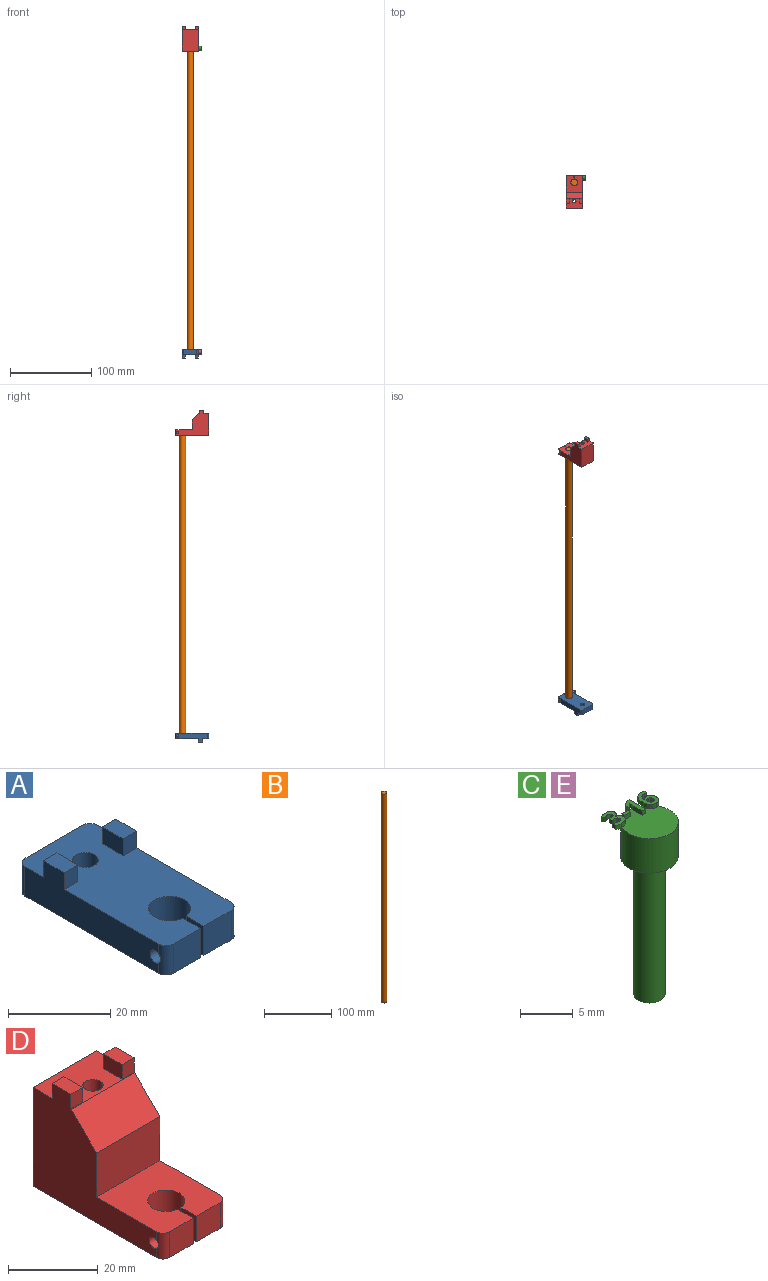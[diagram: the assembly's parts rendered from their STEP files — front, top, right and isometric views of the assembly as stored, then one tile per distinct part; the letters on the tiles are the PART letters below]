
ASSEMBLY  parts=5 mates=4
PART A: 25 faces, bbox 20x41x11 mm
  f0: plane 41x20mm, normal (0,0,1), area 694.2mm2, adj f1,f2,f3,f4,f5,f6,f7,f8
  f1: plane 16x7mm, normal (0,1,0), area 112mm2, adj f0,f10,f21,f24
  f2: plane 37x11mm, normal (-1,0,0), area 276.4mm2, adj f0,f10,f11,f13,f14,f20,f21,f22
  f3: plane 7.5x7mm, normal (0,-1,0), area 52.5mm2, adj f0,f4,f10,f22
  f4: plane 7x4.88mm, normal (1,0,0), area 27.6mm2, adj f0,f3,f5,f10,f20
  f5: cylinder r=4.15mm len=8.3mm, axis (0,0,-1), area 175.5mm2, adj f0,f4,f6,f10
  f6: plane 7x4.88mm, normal (-1,0,0), area 27.6mm2, adj f0,f5,f7,f10,f19
  f7: plane 7.5x7mm, normal (0,-1,0), area 52.5mm2, adj f0,f6,f10,f23
  f8: cylinder r=2.52mm len=7mm, axis (0,0,-1), area 110.8mm2, adj f0,f10
  f9: plane 37x11mm, normal (1,0,0), area 276.4mm2, adj f0,f10,f15,f16,f18,f19,f23,f24
  f10: plane 41x20mm, normal (0,0,-1), area 737.7mm2, adj f1,f2,f3,f4,f5,f6,f7,f8
  f11: plane 4x3.75mm, normal (0,-1,0), area 15mm2, adj f0,f2,f12,f14
  f12: plane 5.8x4mm, normal (1,0,0), area 23.2mm2, adj f0,f11,f13,f14
  f13: plane 4x3.75mm, normal (0,1,0), area 15mm2, adj f0,f2,f12,f14
  f14: plane 5.8x3.75mm, normal (0,0,1), area 21.7mm2, adj f2,f11,f12,f13
  f15: plane 4x3.75mm, normal (0,-1,0), area 15mm2, adj f0,f9,f17,f18
  f16: plane 4x3.75mm, normal (0,1,0), area 15mm2, adj f0,f9,f17,f18
  f17: plane 5.8x4mm, normal (-1,0,0), area 23.2mm2, adj f0,f15,f16,f18
  f18: plane 5.8x3.75mm, normal (0,0,1), area 21.7mm2, adj f9,f15,f16,f17
  f19: cylinder r=1.45mm len=9.5mm, axis (1,0,0), area 86.5mm2, adj f6,f9,f23
  f20: cylinder r=1.45mm len=9.5mm, axis (1,0,0), area 86.5mm2, adj f2,f4,f22
  f21: cylinder r=2mm len=7mm, axis (0,0,-1), area 22mm2, adj f0,f1,f2,f10
  f22: cylinder r=2mm len=7mm, axis (0,0,1), area 21.2mm2, adj f0,f2,f3,f10,f20
  f23: cylinder r=2mm len=7mm, axis (0,0,-1), area 21.2mm2, adj f0,f7,f9,f10,f19
  f24: cylinder r=2mm len=7mm, axis (0,0,1), area 22mm2, adj f0,f1,f9,f10
PART B: 3 faces, bbox 8x8x380 mm
  f0: cylinder r=4mm len=380mm, axis (0,0,-1), area 9550.4mm2, adj f1,f2
  f1: plane 8x8mm, normal (0,0,1), area 50.3mm2, adj f0
  f2: plane 8x8mm, normal (0,0,-1), area 50.3mm2, adj f0
PART C: 79 faces, bbox 6x6.3x20.5 mm
  f0: plane 0.44x0.4mm, normal (0,0,1), area 0.1mm2, adj f2,f68,f69,f70,f71
  f1: plane 5.5x5.5mm, normal (0,0,1), area 21.8mm2, adj f2,f28,f29,f30,f35,f36,f37,f38
  f2: cylinder r=2.75mm len=5.5mm, axis (0,0,-1), area 69.1mm2, adj f0,f1,f3,f6,f51,f78
  f3: plane 5.5x5.5mm, normal (0,0,-1), area 16.7mm2, adj f2,f4
  f4: cylinder r=1.5mm len=16mm, axis (0,0,1), area 150.8mm2, adj f3,f5
  f5: plane 3x3mm, normal (0,0,-1), area 7.1mm2, adj f4
  f6: plane 2.26x1.46mm, normal (0,0,-1), area 1.5mm2, adj f2,f7,f8,f9,f10,f11,f12,f13
  f7: extruded ~0.5x0.35mm, area 0.2mm2, adj f6,f8,f33,f34
  f8: extruded ~0.5x0.38mm, area 0.2mm2, adj f6,f7,f9,f34
  f9: extruded ~0.54x0.5mm, area 0.3mm2, adj f6,f8,f10,f34
  f10: extruded ~0.72x0.5mm, area 0.4mm2, adj f6,f9,f11,f34
  f11: plane 0.5x0.32mm, normal (-0.83,-0.56,0), area 0.2mm2, adj f6,f10,f12,f34
  f12: extruded ~0.5x0.25mm, area 0.1mm2, adj f6,f11,f13,f34
  f13: extruded ~0.5x0.22mm, area 0.1mm2, adj f6,f12,f14,f34
  f14: extruded ~0.5x0.31mm, area 0.2mm2, adj f6,f13,f15,f34
  f15: extruded ~0.5x0.23mm, area 0.1mm2, adj f6,f14,f16,f34
  f16: extruded ~0.5x0.37mm, area 0.2mm2, adj f6,f15,f17,f34
  f17: plane 0.5x0.17mm, normal (0,1,0), area 0.1mm2, adj f6,f16,f18,f34
  f18: plane 0.5x0.36mm, normal (-1,0,0), area 0.2mm2, adj f6,f17,f19,f34
  f19: plane 0.5x0.17mm, normal (0,-1,0), area 0.1mm2, adj f6,f18,f20,f34
  f20: extruded ~0.5x0.4mm, area 0.2mm2, adj f6,f19,f21,f34
  f21: extruded ~0.5x0.22mm, area 0.1mm2, adj f6,f20,f22,f34
  f22: extruded ~0.5x0.25mm, area 0.1mm2, adj f6,f21,f23,f34
  f23: extruded ~0.5x0.34mm, area 0.2mm2, adj f6,f22,f24,f34
  f24: extruded ~0.5x0.3mm, area 0.2mm2, adj f6,f23,f25,f34
  f25: extruded ~0.5x0.28mm, area 0.2mm2, adj f6,f24,f26,f34
  f26: plane 0.5x0.4mm, normal (-1,0,0), area 0.2mm2, adj f6,f25,f27,f34
  f27: extruded ~0.63x0.5mm, area 0.3mm2, adj f6,f26,f28,f34
  f28: extruded ~0.66x0.5mm, area 0.3mm2, adj f1,f6,f27,f29,f34
  f29: extruded ~0.5x0.49mm, area 0.3mm2, adj f1,f28,f30,f34
  f30: extruded ~0.5x0.35mm, area 0.2mm2, adj f1,f6,f29,f31,f34
  f31: extruded ~0.5x0.4mm, area 0.2mm2, adj f6,f30,f32,f34
  f32: plane 0.5x0.01mm, normal (1,0,0), area 0mm2, adj f6,f31,f33,f34
  f33: extruded ~0.5x0.35mm, area 0.2mm2, adj f6,f7,f32,f34
  f34: plane 2.26x1.52mm, normal (0,0,1), area 1.8mm2, adj f7,f8,f9,f10,f11,f12,f13,f14
  f35: plane 0.5x0.38mm, normal (-1,0,0), area 0.2mm2, adj f1,f36,f38,f39
  f36: plane 0.81x0.5mm, normal (0,-1,0), area 0.4mm2, adj f1,f35,f37,f39
  f37: plane 0.5x0.38mm, normal (1,0,0), area 0.2mm2, adj f1,f36,f38,f39
  f38: plane 0.81x0.5mm, normal (0,1,0), area 0.4mm2, adj f1,f35,f37,f39
  f39: plane 0.81x0.38mm, normal (0,0,1), area 0.3mm2, adj f35,f36,f37,f38
  f40: plane 0.5x0.46mm, normal (0,-1,0), area 0.2mm2, adj f1,f41,f49,f50
  f41: plane 2.2x0.5mm, normal (1,0,0), area 1.1mm2, adj f1,f40,f42,f50,f51
  f42: plane 0.5x0.38mm, normal (0,1,0), area 0.2mm2, adj f41,f43,f50,f51
  f43: plane 0.71x0.56mm, normal (-0.62,0.78,0), area 0.5mm2, adj f42,f44,f50,f51
  f44: plane 0.5x0.28mm, normal (-0.78,-0.63,0), area 0.2mm2, adj f1,f43,f45,f50,f51
  f45: plane 0.5x0.25mm, normal (0.63,-0.78,0), area 0.2mm2, adj f1,f44,f46,f50,f51
  f46: extruded ~0.5x0.16mm, area 0.1mm2, adj f45,f47,f50,f51
  f47: plane 0.5x0.23mm, normal (-1,0.03,0), area 0.1mm2, adj f46,f48,f50,f51
  f48: plane 0.5x0.21mm, normal (-1,0.02,0), area 0.1mm2, adj f1,f47,f49,f50,f51
  f49: plane 1.27x0.5mm, normal (-1,0,0), area 0.6mm2, adj f1,f40,f48,f50
  f50: plane 2.2x1.09mm, normal (0,0,1), area 1.2mm2, adj f40,f41,f42,f43,f44,f45,f46,f47
  f51: plane 1.09x0.84mm, normal (0,0,-1), area 0.6mm2, adj f2,f41,f42,f43,f44,f45,f46,f47
  f52: extruded ~0.97x0.5mm, area 0.5mm2, adj f1,f53,f76,f77,f78
  f53: extruded ~0.52x0.5mm, area 0.3mm2, adj f1,f52,f54,f77
  f54: extruded ~0.5x0.33mm, area 0.2mm2, adj f1,f53,f55,f77
  f55: extruded ~0.5x0.42mm, area 0.2mm2, adj f1,f54,f56,f77
  f56: extruded ~0.55x0.5mm, area 0.3mm2, adj f1,f55,f57,f77,f78
  f57: extruded ~0.56x0.5mm, area 0.3mm2, adj f56,f58,f77,f78
  f58: extruded ~0.51x0.5mm, area 0.3mm2, adj f57,f59,f77,f78
  f59: extruded ~0.5x0.46mm, area 0.3mm2, adj f58,f60,f77,f78
  f60: extruded ~0.5x0.48mm, area 0.3mm2, adj f59,f61,f77,f78
  f61: plane 0.5x0.02mm, normal (0,1,0), area 0mm2, adj f60,f62,f77,f78
  f62: extruded ~0.5x0.4mm, area 0.2mm2, adj f61,f63,f77,f78
  f63: extruded ~0.5x0.23mm, area 0.2mm2, adj f62,f64,f77,f78
  f64: extruded ~0.5x0.39mm, area 0.2mm2, adj f63,f65,f77,f78
  f65: extruded ~0.5x0.26mm, area 0.1mm2, adj f64,f66,f77,f78
  f66: plane 0.5x0.37mm, normal (1,0,0), area 0.2mm2, adj f65,f67,f77,f78
  f67: extruded ~0.5x0.29mm, area 0.1mm2, adj f66,f76,f77,f78
  f68: extruded ~0.5x0.23mm, area 0.1mm2, adj f0,f69,f75,f77,f78
  f69: extruded ~0.5x0.24mm, area 0.1mm2, adj f0,f68,f70,f77
  f70: extruded ~0.5x0.3mm, area 0.2mm2, adj f0,f69,f71,f77
  f71: extruded ~0.5x0.21mm, area 0.1mm2, adj f0,f70,f72,f77,f78
  f72: extruded ~0.5x0.24mm, area 0.1mm2, adj f71,f73,f77,f78
  f73: extruded ~0.5x0.22mm, area 0.1mm2, adj f72,f74,f77,f78
  f74: extruded ~0.5x0.25mm, area 0.1mm2, adj f73,f75,f77,f78
  f75: extruded ~0.5x0.28mm, area 0.2mm2, adj f68,f74,f77,f78
  f76: extruded ~0.83x0.5mm, area 0.5mm2, adj f52,f67,f77,f78
  f77: plane 2.25x1.55mm, normal (0,0,1), area 2.1mm2, adj f52,f53,f54,f55,f56,f57,f58,f59
  f78: plane 2.22x1.55mm, normal (0,0,-1), area 1.5mm2, adj f2,f52,f56,f57,f58,f59,f60,f61
PART D: 29 faces, bbox 20x41x31 mm
  f0: plane 21x20mm, normal (0,0,1), area 359.3mm2, adj f1,f3,f4,f5,f6,f7,f8,f12
  f1: plane 39x31mm, normal (1,0,0), area 658.8mm2, adj f0,f2,f9,f10,f13,f14,f16,f21
  f2: plane 27x20mm, normal (0,1,0), area 540mm2, adj f1,f3,f9,f16
  f3: plane 39x31mm, normal (-1,0,0), area 658.8mm2, adj f0,f2,f9,f11,f12,f14,f16,f17
  f4: plane 7.5x7mm, normal (0,-1,0), area 52.5mm2, adj f0,f5,f9,f12
  f5: plane 7x4.88mm, normal (1,0,0), area 27.6mm2, adj f0,f4,f6,f9,f11
  f6: cylinder r=4.15mm len=8.3mm, axis (0,0,-1), area 175.5mm2, adj f0,f5,f7,f9
  f7: plane 7x4.88mm, normal (-1,0,0), area 27.6mm2, adj f0,f6,f8,f9,f10
  f8: plane 7.5x7mm, normal (0,-1,0), area 52.5mm2, adj f0,f7,f9,f13
  f9: plane 41x20mm, normal (0,0,-1), area 680.8mm2, adj f1,f2,f3,f4,f5,f6,f7,f8
  f10: cylinder r=1.45mm len=9.5mm, axis (1,0,0), area 86.5mm2, adj f1,f7,f13
  f11: cylinder r=1.45mm len=9.5mm, axis (1,0,0), area 86.5mm2, adj f3,f5,f12
  f12: cylinder r=2mm len=7mm, axis (0,0,1), area 21.2mm2, adj f0,f3,f4,f9,f11
  f13: cylinder r=2mm len=7mm, axis (0,0,-1), area 21.2mm2, adj f0,f1,f8,f9,f10
  f14: plane 20x12mm, normal (0,-1,0), area 240mm2, adj f0,f1,f3,f25
  f15: cylinder r=2.25mm len=12mm, axis (0,0,-1), area 169.6mm2, adj f16,f27
  f16: plane 20x12mm, normal (0,0,1), area 179.8mm2, adj f1,f2,f3,f15,f17,f18,f19,f21
  f17: plane 4x3.75mm, normal (0,1,0), area 15mm2, adj f3,f16,f18,f20
  f18: plane 5.9x4mm, normal (1,0,0), area 23.6mm2, adj f16,f17,f19,f20
  f19: plane 4x3.75mm, normal (0,-1,0), area 15mm2, adj f3,f16,f18,f20
  f20: plane 5.9x3.75mm, normal (0,0,1), area 22.1mm2, adj f3,f17,f18,f19
  f21: plane 4x3.75mm, normal (0,-1,0), area 15mm2, adj f1,f16,f22,f24
  f22: plane 5.9x4mm, normal (-1,0,0), area 23.6mm2, adj f16,f21,f23,f24
  f23: plane 4x3.75mm, normal (0,1,0), area 15mm2, adj f1,f16,f22,f24
  f24: plane 5.9x3.75mm, normal (0,0,1), area 22.1mm2, adj f1,f21,f22,f23
  f25: plane 20x8mm, normal (0,-0.71,0.71), area 226.3mm2, adj f1,f3,f14,f16
  f26: cylinder r=5mm len=13mm, axis (0,0,-1), area 408.4mm2, adj f9,f28
  f27: plane 6x6mm, normal (0,0,-1), area 12.4mm2, adj f15,f28
  f28: cone r=5mm half-angle=45deg, axis (0,0,-1), area 71.1mm2, adj f26,f27
PART E: same geometry as C
PLACE A rot(axis=(1,0,0),180deg) t=(68.67,74.18,-172.64)mm
PLACE B t=(71.03,65.18,-179.64)mm
PLACE C rot(axis=(0.71,0,0.71),180deg) t=(81.03,71.23,186.86)mm
PLACE D rot(axis=(0,0,1),180deg) t=(74.44,74.18,193.36)mm
PLACE E rot(axis=(0.71,0,0.71),180deg) t=(81.03,71.23,-186.14)mm
MATE fastened B.f0 <-> D.f6  axis (0,0,1) through (71.03,65.18,200.36)mm
MATE fastened B.f0 <-> A.f5  axis (0,0,-1) through (71.03,65.18,-179.64)mm
MATE fastened E.f2 <-> A.f19  axis (-1,0,0) through (81.03,71.23,-176.14)mm
MATE fastened C.f2 <-> D.f10  axis (-1,0,0) through (81.03,71.23,196.86)mm
